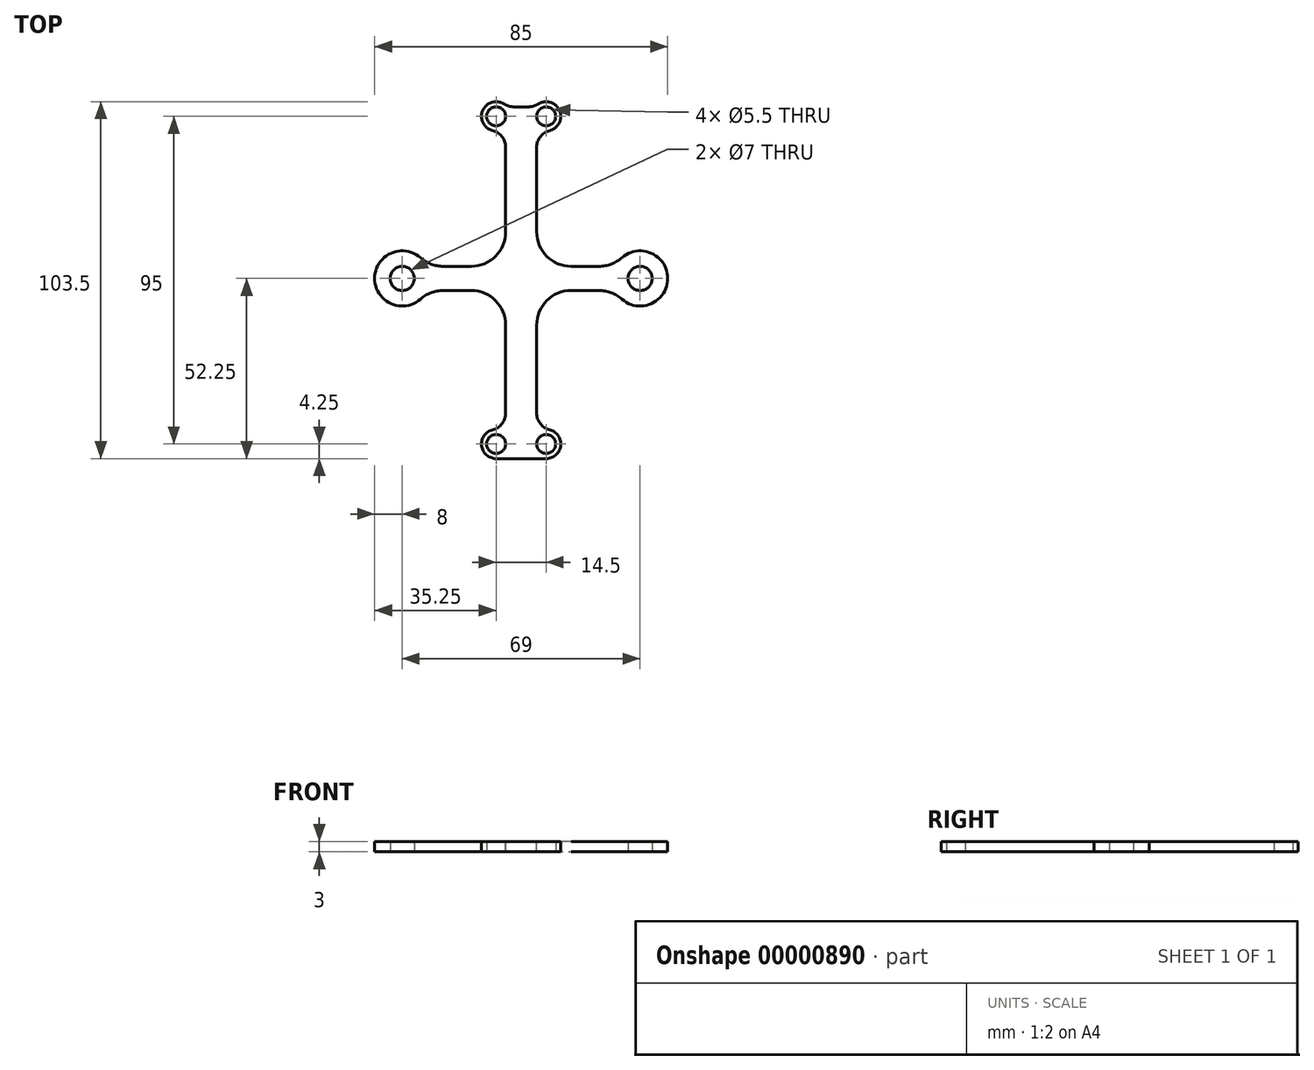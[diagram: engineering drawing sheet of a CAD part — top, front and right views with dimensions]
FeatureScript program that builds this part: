
annotation { "Feature Type Name" : "Feature", "Feature Type Description" : "" }
export const myFeature = defineFeature(function(context is Context, id is Id, definition is map)
    precondition{}
    {
        {
            var Q0;
            Q0=qCreatedBy(makeId("Top.planeOp"),FACE);
            var sketch = newSketch(context, id + "F0", { "sketchPlane" : qUnion([Q0])});
            skLineSegment(sketch, "E0.bottom", {"start": v(-31.17, -57.58) * mm, "end": v(37.83, -57.58) * mm, "construction": true});
            skLineSegment(sketch, "E0.top", {"start": v(-31.17, 37.42) * mm, "end": v(37.83, 37.42) * mm, "construction": true});
            skLineSegment(sketch, "E0.left", {"start": v(-31.17, -57.58) * mm, "end": v(-31.17, 37.42) * mm, "construction": true});
            skLineSegment(sketch, "E0.right", {"start": v(37.83, -57.58) * mm, "end": v(37.83, 37.42) * mm, "construction": true});
            skLineSegment(sketch, "E1", {"start": v(3.33, 37.42) * mm, "end": v(3.33, -57.58) * mm, "construction": true});
            skLineSegment(sketch, "E2", {"start": v(3.33, 37.42) * mm, "end": v(3.33, -15.58) * mm, "construction": true});
            skLineSegment(sketch, "E3", {"start": v(3.33, -15.58) * mm, "end": v(37.83, -15.58) * mm, "construction": true});
            skCircle(sketch, "E4", {"center": v(37.83, -15.58) * mm, "radius": 3.5 * mm});
            skLineSegment(sketch, "E5", {"start": v(3.33, -15.58) * mm, "end": v(-31.17, -15.58) * mm, "construction": true});
            skCircle(sketch, "E6", {"center": v(-31.17, -15.58) * mm, "radius": 3.5 * mm});
            skLineSegment(sketch, "E7", {"start": v(-31.17, -15.58) * mm, "end": v(-31.17, -60.58) * mm, "construction": true});
            skLineSegment(sketch, "E8", {"start": v(11.33, -54.78) * mm, "end": v(11.33, -59.78) * mm, "construction": true});
            skLineSegment(sketch, "E9", {"start": v(11.33, -59.78) * mm, "end": v(6.33, -59.78) * mm, "construction": true});
            skLineSegment(sketch, "E10", {"start": v(3.33, 37.42) * mm, "end": v(3.33, 31.42) * mm, "construction": true});
            skLineSegment(sketch, "E11", {"start": v(3.33, 31.42) * mm, "end": v(10.58, 31.42) * mm, "construction": true});
            skLineSegment(sketch, "E12", {"start": v(3.33, 31.42) * mm, "end": v(-3.92, 31.42) * mm, "construction": true});
            skCircle(sketch, "E13", {"center": v(-3.92, 31.42) * mm, "radius": 2.75 * mm});
            skCircle(sketch, "E14", {"center": v(10.58, 31.42) * mm, "radius": 2.75 * mm});
            skLineSegment(sketch, "E15", {"start": v(-3.92, 31.42) * mm, "end": v(-3.92, -63.58) * mm, "construction": true});
            skLineSegment(sketch, "E16", {"start": v(10.58, 31.42) * mm, "end": v(10.58, -63.58) * mm, "construction": true});
            skCircle(sketch, "E17", {"center": v(-3.92, -63.58) * mm, "radius": 2.75 * mm});
            skCircle(sketch, "E18", {"center": v(10.58, -63.58) * mm, "radius": 2.75 * mm});
            skLineSegment(sketch, "E19.0", {"start": v(-45.05, -103.33) * mm, "end": v(-45.05, -103.33) * mm});
            skCircle(sketch, "E20", {"center": v(-31.17, -15.58) * mm, "radius": 8 * mm});
            skCircle(sketch, "E21", {"center": v(37.83, -15.58) * mm, "radius": 8 * mm});
            skCircle(sketch, "E22", {"center": v(10.58, 31.42) * mm, "radius": 4.25 * mm});
            skCircle(sketch, "E23", {"center": v(-3.92, 31.42) * mm, "radius": 4.25 * mm});
            skCircle(sketch, "E24", {"center": v(10.58, -63.58) * mm, "radius": 4.25 * mm});
            skCircle(sketch, "E25", {"center": v(-3.92, -63.58) * mm, "radius": 4.25 * mm});
            skLineSegment(sketch, "E26", {"start": v(-3.92, 34.17) * mm, "end": v(10.58, 34.17) * mm});
            skLineSegment(sketch, "E27", {"start": v(-31.17, -12.08) * mm, "end": v(37.83, -12.08) * mm});
            skLineSegment(sketch, "E28", {"start": v(37.83, -19.08) * mm, "end": v(-31.17, -19.08) * mm});
            skLineSegment(sketch, "E29", {"start": v(-1.17, 31.42) * mm, "end": v(-1.17, -63.58) * mm});
            skLineSegment(sketch, "E30", {"start": v(7.83, -63.58) * mm, "end": v(7.83, 31.42) * mm});
            skLineSegment(sketch, "E31", {"start": v(-3.92, -67.83) * mm, "end": v(10.58, -67.83) * mm});
            skSolve(sketch);
        }
        {
            var Q0;
            {var subQ0=sQuery(id+"F0.wireOp",EDGE,"E26");var subQ1=sQuery(id+"F0.wireOp",EDGE,"E13");var subQ2=makeQuery(id+"F0.imprint","INTERSECT",VERTEX,{"derivedFrom":[subQ1,subQ0]});Q0=makeQuery(id+"F0.imprint","IMPRINT",FACE,{"disambiguationData":[TD([[makeQuery(id+"F0.imprint","IMPRINT",EDGE,{"disambiguationData":[TD([[subQ2,1.0]])],"derivedFrom":subQ1}),-1.0]])]});}
            var Q1;
            {var subQ0=sQuery(id+"F0.wireOp",EDGE,"E26");var subQ1=sQuery(id+"F0.wireOp",EDGE,"E13");var subQ2=makeQuery(id+"F0.imprint","INTERSECT",VERTEX,{"derivedFrom":[subQ1,subQ0]});Q1=makeQuery(id+"F0.imprint","IMPRINT",FACE,{"disambiguationData":[TD([[makeQuery(id+"F0.imprint","IMPRINT",EDGE,{"disambiguationData":[TD([[subQ2,-1.0]])],"derivedFrom":subQ1}),-1.0]])]});}
            var Q2;
            {var subQ0=sQuery(id+"F0.wireOp",EDGE,"E26");var subQ1=sQuery(id+"F0.wireOp",EDGE,"E14");var subQ2=makeQuery(id+"F0.imprint","INTERSECT",VERTEX,{"derivedFrom":[subQ1,subQ0]});Q2=makeQuery(id+"F0.imprint","IMPRINT",FACE,{"disambiguationData":[TD([[makeQuery(id+"F0.imprint","IMPRINT",EDGE,{"disambiguationData":[TD([[subQ2,1.0]])],"derivedFrom":subQ1}),-1.0]])]});}
            var Q3;
            {var subQ0=sQuery(id+"F0.wireOp",EDGE,"E26");var subQ1=sQuery(id+"F0.wireOp",EDGE,"E14");var subQ2=makeQuery(id+"F0.imprint","INTERSECT",VERTEX,{"derivedFrom":[subQ1,subQ0]});Q3=makeQuery(id+"F0.imprint","IMPRINT",FACE,{"disambiguationData":[TD([[makeQuery(id+"F0.imprint","IMPRINT",EDGE,{"disambiguationData":[TD([[subQ2,-1.0]])],"derivedFrom":subQ1}),-1.0]])]});}
            var Q4;
            {var subQ5=sQuery(id+"F0.wireOp",EDGE,"E26");var subQ9=sQuery(id+"F0.wireOp",EDGE,"E22");var subQ10=makeQuery(id+"F0.imprint","INTERSECT",VERTEX,{"derivedFrom":[subQ9,subQ5]});Q4=makeQuery(id+"F0.imprint","IMPRINT",FACE,{"disambiguationData":[TD([[makeQuery(id+"F0.imprint","IMPRINT",EDGE,{"disambiguationData":[TD([[subQ10,-1.0]])],"derivedFrom":subQ9}),-1.0]])]});}
            var Q5;
            {var subQ0=sQuery(id+"F0.wireOp",EDGE,"E27");var subQ1=sQuery(id+"F0.wireOp",EDGE,"E6");var subQ2=makeQuery(id+"F0.imprint","INTERSECT",VERTEX,{"derivedFrom":[subQ1,subQ0]});Q5=makeQuery(id+"F0.imprint","IMPRINT",FACE,{"disambiguationData":[TD([[makeQuery(id+"F0.imprint","IMPRINT",EDGE,{"disambiguationData":[TD([[subQ2,-1.0]])],"derivedFrom":subQ1}),-1.0]])]});}
            var Q6;
            {var subQ0=sQuery(id+"F0.wireOp",EDGE,"E27");var subQ1=sQuery(id+"F0.wireOp",EDGE,"E20");var subQ2=makeQuery(id+"F0.imprint","INTERSECT",VERTEX,{"derivedFrom":[subQ1,subQ0]});Q6=makeQuery(id+"F0.imprint","IMPRINT",FACE,{"disambiguationData":[TD([[makeQuery(id+"F0.imprint","IMPRINT",EDGE,{"disambiguationData":[TD([[subQ2,1.0]])],"derivedFrom":subQ1}),-1.0]])]});}
            var Q7;
            {var subQ0=sQuery(id+"F0.wireOp",EDGE,"E27");var subQ1=sQuery(id+"F0.wireOp",EDGE,"E6");var subQ2=makeQuery(id+"F0.imprint","INTERSECT",VERTEX,{"derivedFrom":[subQ1,subQ0]});Q7=makeQuery(id+"F0.imprint","IMPRINT",FACE,{"disambiguationData":[TD([[makeQuery(id+"F0.imprint","IMPRINT",EDGE,{"disambiguationData":[TD([[subQ2,1.0]])],"derivedFrom":subQ1}),-1.0]])]});}
            var Q8;
            {var subQ0=sQuery(id+"F0.wireOp",EDGE,"E29");var subQ1=sQuery(id+"F0.wireOp",EDGE,"E27");var subQ2=makeQuery(id+"F0.imprint","INTERSECT",VERTEX,{"derivedFrom":[subQ1,subQ0]});Q8=makeQuery(id+"F0.imprint","IMPRINT",FACE,{"disambiguationData":[TD([[makeQuery(id+"F0.imprint","IMPRINT",EDGE,{"disambiguationData":[TD([[subQ2,-1.0]])],"derivedFrom":subQ1}),-1.0]])]});}
            var Q9;
            {var subQ0=sQuery(id+"F0.wireOp",EDGE,"E27");var subQ1=sQuery(id+"F0.wireOp",EDGE,"E21");var subQ2=makeQuery(id+"F0.imprint","INTERSECT",VERTEX,{"derivedFrom":[subQ1,subQ0]});Q9=makeQuery(id+"F0.imprint","IMPRINT",FACE,{"disambiguationData":[TD([[makeQuery(id+"F0.imprint","IMPRINT",EDGE,{"disambiguationData":[TD([[subQ2,-1.0]])],"derivedFrom":subQ1}),-1.0]])]});}
            var Q10;
            {var subQ0=sQuery(id+"F0.wireOp",EDGE,"E27");var subQ1=sQuery(id+"F0.wireOp",EDGE,"E4");var subQ2=makeQuery(id+"F0.imprint","INTERSECT",VERTEX,{"derivedFrom":[subQ1,subQ0]});Q10=makeQuery(id+"F0.imprint","IMPRINT",FACE,{"disambiguationData":[TD([[makeQuery(id+"F0.imprint","IMPRINT",EDGE,{"disambiguationData":[TD([[subQ2,-1.0]])],"derivedFrom":subQ1}),-1.0]])]});}
            var Q11;
            {var subQ0=sQuery(id+"F0.wireOp",EDGE,"E27");var subQ1=sQuery(id+"F0.wireOp",EDGE,"E4");var subQ2=makeQuery(id+"F0.imprint","INTERSECT",VERTEX,{"derivedFrom":[subQ1,subQ0]});Q11=makeQuery(id+"F0.imprint","IMPRINT",FACE,{"disambiguationData":[TD([[makeQuery(id+"F0.imprint","IMPRINT",EDGE,{"disambiguationData":[TD([[subQ2,1.0]])],"derivedFrom":subQ1}),-1.0]])]});}
            var Q12;
            {var subQ0=sQuery(id+"F0.wireOp",EDGE,"455b8331-9871-4dfb-9193-c4615e9f80b4");var subQ1=sQuery(id+"F0.wireOp",EDGE,"E24");var subQ2=makeQuery(id+"F0.imprint","INTERSECT",VERTEX,{"derivedFrom":[subQ1,subQ0]});Q12=makeQuery(id+"F0.imprint","IMPRINT",FACE,{"disambiguationData":[TD([[makeQuery(id+"F0.imprint","IMPRINT",EDGE,{"disambiguationData":[TD([[subQ2,1.0]])],"derivedFrom":subQ1}),-1.0]])]});}
            var Q13;
            {var subQ0=sQuery(id+"F0.wireOp",EDGE,"090fccfc-c7a4-420f-a817-da86fd9ed7b5");Q13=makeQuery(id+"F0.imprint","IMPRINT",FACE,{"disambiguationData":[TD([[makeQuery(id+"F0.imprint","IMPRINT",EDGE,{"derivedFrom":subQ0}),-1.0]])]});}
            var Q14;
            {var subQ2=sQuery(id+"F0.wireOp",EDGE,"455b8331-9871-4dfb-9193-c4615e9f80b4");var subQ6=sQuery(id+"F0.wireOp",EDGE,"E17");var subQ9=makeQuery(id+"F0.imprint","INTERSECT",VERTEX,{"derivedFrom":[subQ6,subQ2]});Q14=makeQuery(id+"F0.imprint","IMPRINT",FACE,{"disambiguationData":[TD([[makeQuery(id+"F0.imprint","IMPRINT",EDGE,{"disambiguationData":[TD([[subQ9,1.0]])],"derivedFrom":subQ6}),-1.0]])]});}
            var Q15;
            {var subQ0=sQuery(id+"F0.wireOp",EDGE,"455b8331-9871-4dfb-9193-c4615e9f80b4");var subQ1=sQuery(id+"F0.wireOp",EDGE,"E17");var subQ2=makeQuery(id+"F0.imprint","INTERSECT",VERTEX,{"derivedFrom":[subQ1,subQ0]});Q15=makeQuery(id+"F0.imprint","IMPRINT",FACE,{"disambiguationData":[TD([[makeQuery(id+"F0.imprint","IMPRINT",EDGE,{"disambiguationData":[TD([[subQ2,-1.0]])],"derivedFrom":subQ1}),-1.0]])]});}
            var Q16;
            {var subQ0=sQuery(id+"F0.wireOp",EDGE,"455b8331-9871-4dfb-9193-c4615e9f80b4");var subQ1=sQuery(id+"F0.wireOp",EDGE,"E18");var subQ2=makeQuery(id+"F0.imprint","INTERSECT",VERTEX,{"derivedFrom":[subQ1,subQ0]});Q16=makeQuery(id+"F0.imprint","IMPRINT",FACE,{"disambiguationData":[TD([[makeQuery(id+"F0.imprint","IMPRINT",EDGE,{"disambiguationData":[TD([[subQ2,1.0]])],"derivedFrom":subQ1}),-1.0]])]});}
            var Q17;
            {var subQ0=sQuery(id+"F0.wireOp",EDGE,"455b8331-9871-4dfb-9193-c4615e9f80b4");var subQ1=sQuery(id+"F0.wireOp",EDGE,"E18");var subQ2=makeQuery(id+"F0.imprint","INTERSECT",VERTEX,{"derivedFrom":[subQ1,subQ0]});Q17=makeQuery(id+"F0.imprint","IMPRINT",FACE,{"disambiguationData":[TD([[makeQuery(id+"F0.imprint","IMPRINT",EDGE,{"disambiguationData":[TD([[subQ2,-1.0]])],"derivedFrom":subQ1}),-1.0]])]});}
            var Q18;
            {var subQ0=sQuery(id+"F0.wireOp",EDGE,"E31");Q18=makeQuery(id+"F0.imprint","IMPRINT",FACE,{"disambiguationData":[TD([[makeQuery(id+"F0.imprint","IMPRINT",EDGE,{"derivedFrom":subQ0}),1.0]])]});}
            var Q19;
            {var subQ0=sQuery(id+"F0.wireOp",EDGE,"E30");var subQ1=sQuery(id+"F0.wireOp",EDGE,"E28");var subQ2=makeQuery(id+"F0.imprint","INTERSECT",VERTEX,{"derivedFrom":[subQ1,subQ0]});Q19=makeQuery(id+"F0.imprint","IMPRINT",FACE,{"disambiguationData":[TD([[makeQuery(id+"F0.imprint","IMPRINT",EDGE,{"disambiguationData":[TD([[subQ2,-1.0]])],"derivedFrom":subQ1}),1.0]])]});}
            var Q20;
            {var subQ0=sQuery(id+"F0.wireOp",EDGE,"a8c75f21-8b49-408d-b769-a232f3447a95");var subQ3=sQuery(id+"F0.wireOp",EDGE,"E29");var subQ5=makeQuery(id+"F0.imprint","INTERSECT",VERTEX,{"derivedFrom":[subQ3,subQ0]});Q20=makeQuery(id+"F0.imprint","IMPRINT",FACE,{"disambiguationData":[TD([[makeQuery(id+"F0.imprint","IMPRINT",EDGE,{"disambiguationData":[TD([[subQ5,-1.0]])],"derivedFrom":subQ3}),-1.0]])]});}
            var Q21;
            {var subQ0=sQuery(id+"F0.wireOp",EDGE,"a8c75f21-8b49-408d-b769-a232f3447a95");var subQ1=sQuery(id+"F0.wireOp",EDGE,"E24");var subQ2=makeQuery(id+"F0.imprint","INTERSECT",VERTEX,{"derivedFrom":[subQ1,subQ0]});Q21=makeQuery(id+"F0.imprint","IMPRINT",FACE,{"disambiguationData":[TD([[makeQuery(id+"F0.imprint","IMPRINT",EDGE,{"disambiguationData":[TD([[subQ2,-1.0]])],"derivedFrom":subQ1}),-1.0]])]});}
            extrude(context, id + "F1", {"entities" : qUnion([Q0, Q1, Q2, Q3, Q4, Q5, Q6, Q7, Q8, Q9, Q10, Q11, Q12, Q13, Q14, Q15, Q16, Q17, Q18, Q19, Q20, Q21]), "depth" : 3 * mm});
        }
        {
            var Q0;
            Q0=makeQuery(id+"F1.opExtrude","SWEPT_EDGE",EDGE,{"disambiguationData":[OSD([sQuery(id+"F0.wireOp",EDGE,"E27"),sQuery(id+"F0.wireOp",EDGE,"E29")])]});
            var Q1;
            Q1=makeQuery(id+"F1.opExtrude","SWEPT_EDGE",EDGE,{"disambiguationData":[OSD([sQuery(id+"F0.wireOp",EDGE,"E28"),sQuery(id+"F0.wireOp",EDGE,"E29")])]});
            var Q2;
            Q2=makeQuery(id+"F1.opExtrude","SWEPT_EDGE",EDGE,{"disambiguationData":[OSD([sQuery(id+"F0.wireOp",EDGE,"E28"),sQuery(id+"F0.wireOp",EDGE,"E30")])]});
            var Q3;
            Q3=makeQuery(id+"F1.opExtrude","SWEPT_EDGE",EDGE,{"disambiguationData":[OSD([sQuery(id+"F0.wireOp",EDGE,"E27"),sQuery(id+"F0.wireOp",EDGE,"E30")])]});
            fillet(context, id + "F2", {"entities" : qUnion([Q0, Q1, Q2, Q3]), "radius" : 10 * mm, "tangentPropagation" : true, "allowEdgeOverflow" : false});
        }
        {
            var Q0;
            Q0=makeQuery(id+"F1.opExtrude","SWEPT_EDGE",EDGE,{"disambiguationData":[OSD([sQuery(id+"F0.wireOp",EDGE,"E20"),sQuery(id+"F0.wireOp",EDGE,"E27")])]});
            var Q1;
            Q1=makeQuery(id+"F1.opExtrude","SWEPT_EDGE",EDGE,{"disambiguationData":[OSD([sQuery(id+"F0.wireOp",EDGE,"E20"),sQuery(id+"F0.wireOp",EDGE,"E28")])]});
            var Q2;
            Q2=makeQuery(id+"F1.opExtrude","SWEPT_EDGE",EDGE,{"disambiguationData":[OSD([sQuery(id+"F0.wireOp",EDGE,"E21"),sQuery(id+"F0.wireOp",EDGE,"E27")])]});
            var Q3;
            Q3=makeQuery(id+"F1.opExtrude","SWEPT_EDGE",EDGE,{"disambiguationData":[OSD([sQuery(id+"F0.wireOp",EDGE,"E21"),sQuery(id+"F0.wireOp",EDGE,"E28")])]});
            fillet(context, id + "F3", {"entities" : qUnion([Q0, Q1, Q2, Q3]), "radius" : 10 * mm, "tangentPropagation" : true, "allowEdgeOverflow" : false});
        }
        {
            var Q0;
            Q0=makeQuery(id+"F1.opExtrude","SWEPT_EDGE",EDGE,{"disambiguationData":[OSD([sQuery(id+"F0.wireOp",EDGE,"E23"),sQuery(id+"F0.wireOp",EDGE,"E29")])]});
            var Q1;
            Q1=makeQuery(id+"F1.opExtrude","SWEPT_EDGE",EDGE,{"disambiguationData":[OSD([sQuery(id+"F0.wireOp",EDGE,"E22"),sQuery(id+"F0.wireOp",EDGE,"E30")])]});
            fillet(context, id + "F4", {"entities" : qUnion([Q0, Q1]), "radius" : 5 * mm, "tangentPropagation" : true, "allowEdgeOverflow" : false});
        }
        {
            var Q0;
            Q0=makeQuery(id+"F1.opExtrude","SWEPT_EDGE",EDGE,{"disambiguationData":[OSD([sQuery(id+"F0.wireOp",EDGE,"E22"),sQuery(id+"F0.wireOp",EDGE,"E26")])]});
            var Q1;
            Q1=makeQuery(id+"F1.opExtrude","SWEPT_EDGE",EDGE,{"disambiguationData":[OSD([sQuery(id+"F0.wireOp",EDGE,"E23"),sQuery(id+"F0.wireOp",EDGE,"E26")])]});
            fillet(context, id + "F5", {"entities" : qUnion([Q0, Q1]), "radius" : 5 * mm, "tangentPropagation" : true, "allowEdgeOverflow" : false});
        }
        {
            var Q0;
            Q0=makeQuery(id+"F1.opExtrude","SWEPT_EDGE",EDGE,{"disambiguationData":[OSD([sQuery(id+"F0.wireOp",EDGE,"E29"),sQuery(id+"F0.wireOp",EDGE,"a8c75f21-8b49-408d-b769-a232f3447a95")])]});
            var Q1;
            Q1=makeQuery(id+"F1.opExtrude","SWEPT_EDGE",EDGE,{"disambiguationData":[OSD([sQuery(id+"F0.wireOp",EDGE,"E30"),sQuery(id+"F0.wireOp",EDGE,"a8c75f21-8b49-408d-b769-a232f3447a95")])]});
            fillet(context, id + "F6", {"entities" : qUnion([Q0, Q1]), "radius" : 5 * mm, "tangentPropagation" : true, "allowEdgeOverflow" : false});
        }
    });
